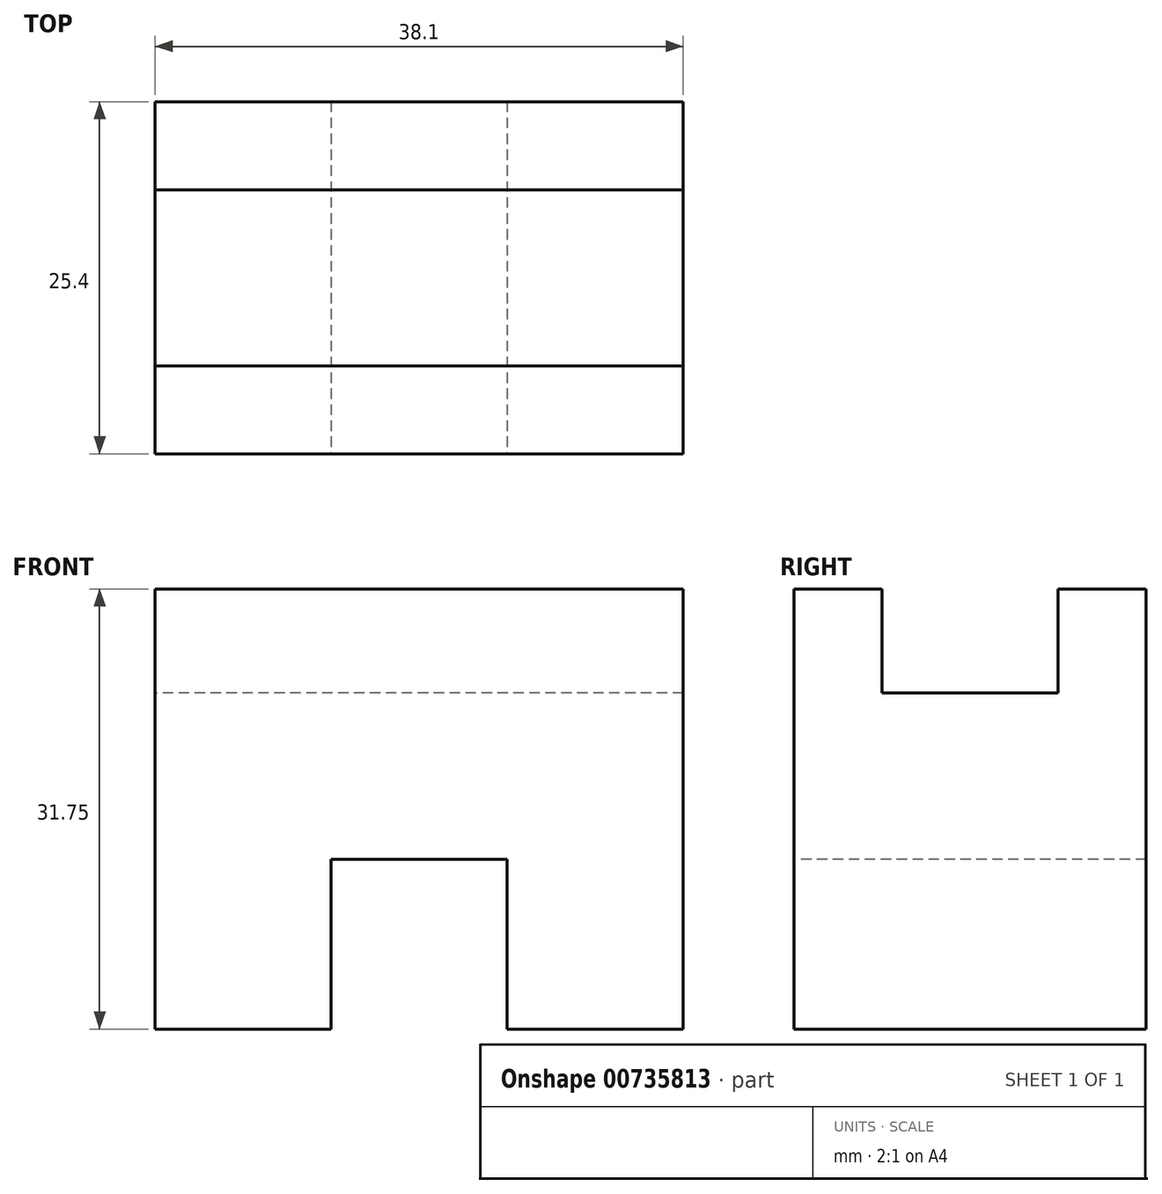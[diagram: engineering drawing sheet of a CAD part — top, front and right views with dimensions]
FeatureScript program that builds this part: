
annotation { "Feature Type Name" : "Feature", "Feature Type Description" : "" }
export const myFeature = defineFeature(function(context is Context, id is Id, definition is map)
    precondition{}
    {
        {
            var Q0;
            Q0=qCreatedBy(makeId("Right.planeOp"),FACE);
            var sketch = newSketch(context, id + "F0", { "sketchPlane" : qUnion([Q0])});
            skLineSegment(sketch, "E0", {"start": v(0, 0) * mm, "end": v(0, 31.75) * mm});
            skLineSegment(sketch, "E1", {"start": v(0, 31.75) * mm, "end": v(6.35, 31.75) * mm});
            skLineSegment(sketch, "E2", {"start": v(6.35, 31.75) * mm, "end": v(6.35, 24.24) * mm});
            skLineSegment(sketch, "E3", {"start": v(6.35, 24.24) * mm, "end": v(19.05, 24.24) * mm});
            skLineSegment(sketch, "E4", {"start": v(19.05, 24.24) * mm, "end": v(19.05, 31.75) * mm});
            skLineSegment(sketch, "E5", {"start": v(19.05, 31.75) * mm, "end": v(25.4, 31.75) * mm});
            skLineSegment(sketch, "E6", {"start": v(25.4, 31.75) * mm, "end": v(25.4, 0) * mm});
            skLineSegment(sketch, "E7", {"start": v(25.4, 0) * mm, "end": v(0, 0) * mm});
            skSolve(sketch);
        }
        {
            var Q0;
            Q0 = qSketchRegion(id + "F0", true);
            extrude(context, id + "F1", {"entities" : qUnion([Q0]), "depth" : 38.1 * mm, "offsetDistance" : 25.4 * mm});
        }
        {
            var Q0;
            Q0=makeQuery(id+"F1.opExtrude","SWEPT_FACE",FACE,{"disambiguationData":[OSD([sQuery(id+"F0.wireOp",EDGE,"E0")])]});
            var sketch = newSketch(context, id + "F2", { "sketchPlane" : qUnion([Q0])});
            skLineSegment(sketch, "E8", {"start": v(12.7, 0) * mm, "end": v(12.7, 12.25) * mm});
            skLineSegment(sketch, "E9", {"start": v(12.7, 12.25) * mm, "end": v(25.4, 12.25) * mm});
            skLineSegment(sketch, "E10", {"start": v(25.4, 12.25) * mm, "end": v(25.4, 0) * mm});
            skLineSegment(sketch, "E11", {"start": v(25.4, 0) * mm, "end": v(12.7, 0) * mm});
            skSolve(sketch);
        }
        {
            var Q0;
            Q0 = qSketchRegion(id + "F2", true);
            extrude(context, id + "F3", {"entities" : qUnion([Q0]), "operationType" : NewBodyOperationType.REMOVE, "oppositeDirection" : true, "depth" : 76.2 * mm, "offsetDistance" : 25.4 * mm});
        }
    });
